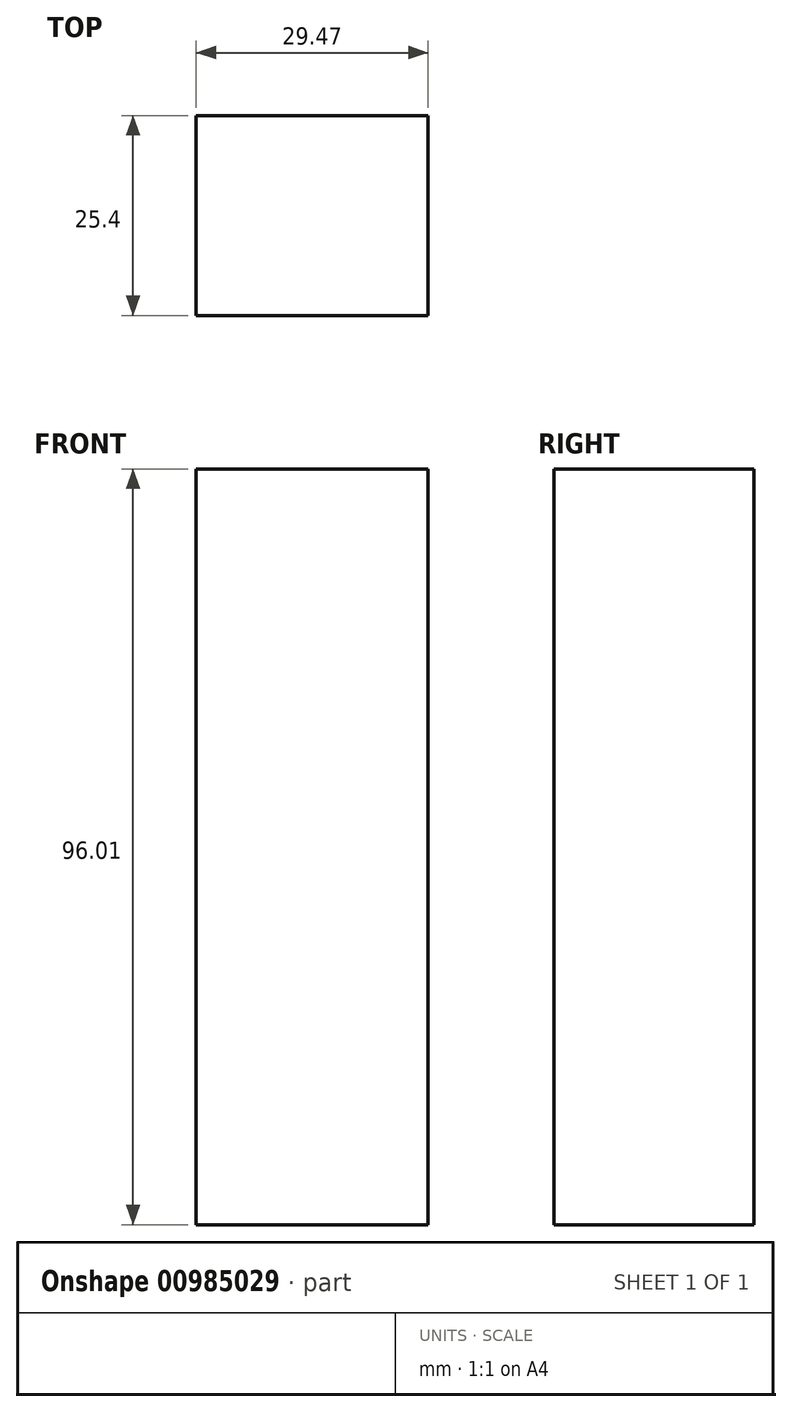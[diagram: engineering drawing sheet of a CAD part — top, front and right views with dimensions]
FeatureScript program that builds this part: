
annotation { "Feature Type Name" : "Feature", "Feature Type Description" : "" }
export const myFeature = defineFeature(function(context is Context, id is Id, definition is map)
    precondition{}
    {
        {
            var Q0;
            Q0=qCreatedBy(makeId("Front.planeOp"),FACE);
            var sketch = newSketch(context, id + "F0", { "sketchPlane" : qUnion([Q0])});
            skLineSegment(sketch, "E0.bottom", {"start": v(41.53, -62.66) * mm, "end": v(71, -62.66) * mm});
            skLineSegment(sketch, "E0.top", {"start": v(41.53, 33.35) * mm, "end": v(71, 33.35) * mm});
            skLineSegment(sketch, "E0.left", {"start": v(41.53, -62.66) * mm, "end": v(41.53, 33.35) * mm});
            skLineSegment(sketch, "E0.right", {"start": v(71, -62.66) * mm, "end": v(71, 33.35) * mm});
            skPoint(sketch, "E0.middle", {"position": v(56.26, -14.66) * mm});
            skSolve(sketch);
        }
        {
            var Q0;
            Q0=makeQuery(id+"F0.imprint","IMPRINT",FACE,{"disambiguationData":[TD([[makeQuery(id+"F0.imprint","IMPRINT",EDGE,{"derivedFrom":sQuery(id+"F0.wireOp",EDGE,"E0.bottom")}),1.0]])]});
            extrude(context, id + "F1", {"entities" : qUnion([Q0]), "depth" : 25.4 * mm, "offsetDistance" : 25.4 * mm});
        }
    });
